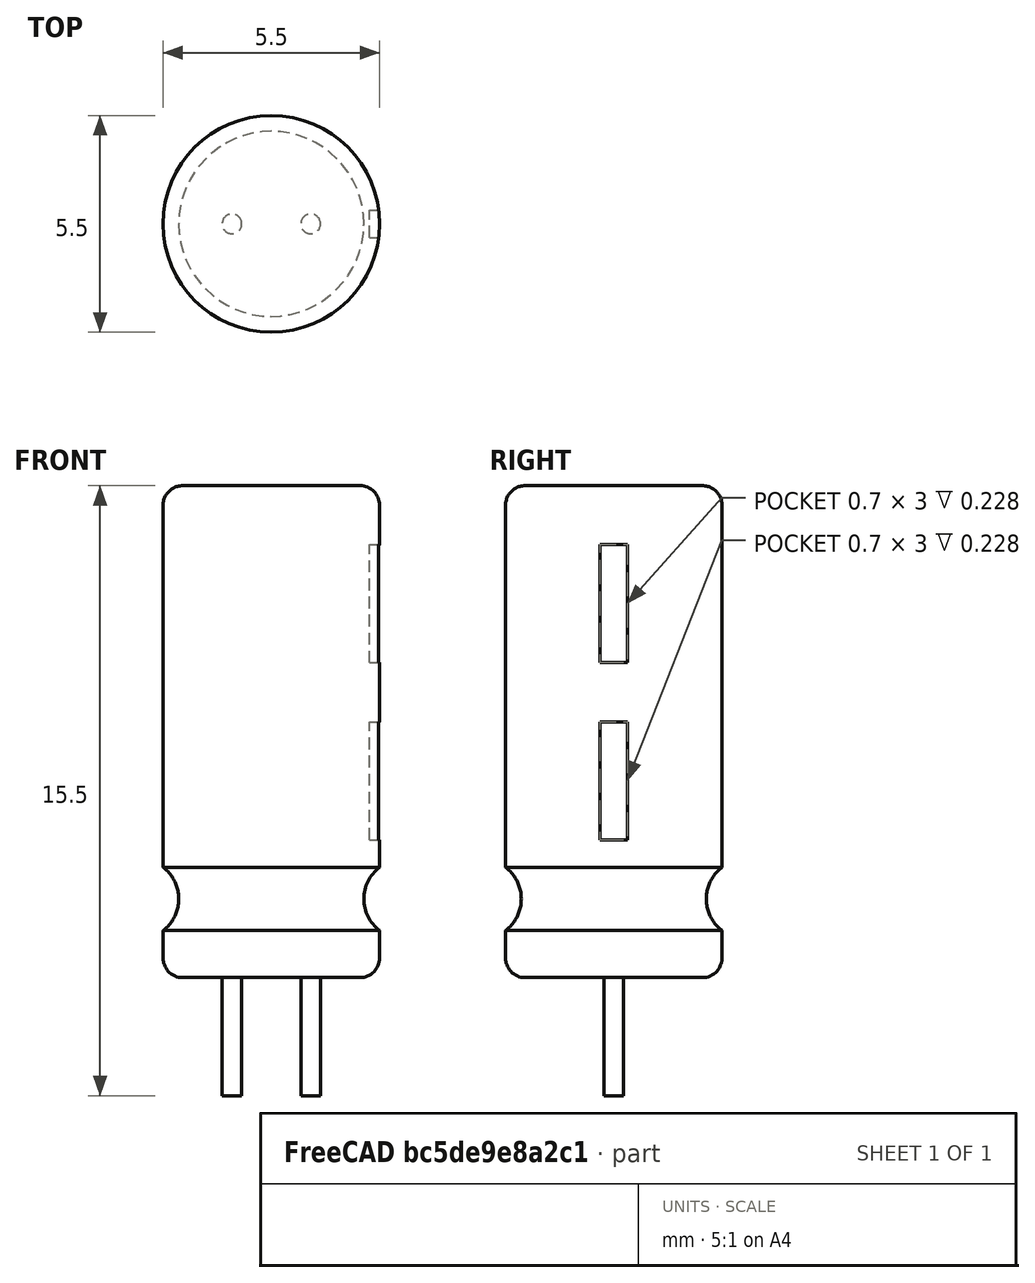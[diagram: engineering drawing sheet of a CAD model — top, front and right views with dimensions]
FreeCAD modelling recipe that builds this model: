
FCSTD DOCUMENT
Label: CAPPR200W50D500H1100
objects: Part::Cylinder×3, Part::Cut×3, Part::Box×2, Part::Fuse×2, Part::Fillet×1, Part::Torus×1
note: 12 computed .brp shape members not serialized (recipe doc carries the construction recipe); baked Part::Feature solids carry a one-line shape summary decoded from their .brp

FEATURE [Part::Cylinder] Cylinder  label="Grundkoerper"
  Angle = 360
  Height = 12.5
  Radius = 2.75
FEATURE [Part::Cylinder] Cylinder001  label="Pin1+"
  Angle = 360
  Height = 3
  Placement = pos=(-1,0,-3) rot=(0,0,1;0rad)
  Radius = 0.25
FEATURE [Part::Cylinder] Cylinder002  label="Pin2-"
  Angle = 360
  Height = 3
  Placement = pos=(1,0,-3) rot=(0,0,1;0rad)
  Radius = 0.25
FEATURE [Part::Fillet] Fillet  label="Abgerundeter Grundkoerper"
  Base = -> Cylinder
  Edges = 2 edges r=0.5: [Edge1,Edge3]
FEATURE [Part::Torus] Torus  label="Ring"
  Angle1 = -180
  Angle2 = 180
  Angle3 = 360
  Placement = pos=(0,0,2) rot=(0,0,1;0rad)
  Radius1 = 3.35
  Radius2 = 1
FEATURE [Part::Cut] Cut  label="Beringter kondensator"
  Base = -> Fillet
  Tool = -> Torus
FEATURE [Part::Box] Box  label="minuszeichen1"
  Height = 3
  Length = 1
  Placement = pos=(2.5,-0.35,3.5) rot=(0,0,1;0rad)
  Width = 0.7
FEATURE [Part::Box] Box001  label="minuszeichen2"
  Height = 3
  Length = 1
  Placement = pos=(2.5,-0.35,8) rot=(0,0,1;0rad)
  Width = 0.7
FEATURE [Part::Cut] Cut001
  Base = -> Cut
  Tool = -> Box
FEATURE [Part::Cut] Cut002
  Base = -> Cut001
  Tool = -> Box001
FEATURE [Part::Fuse] Fusion
  Base = -> Cut002
  Tool = -> Cylinder001
FEATURE [Part::Fuse] Fusion001  label="CAPPR200W50D500H1100"
  Base = -> Fusion
  Tool = -> Cylinder002
